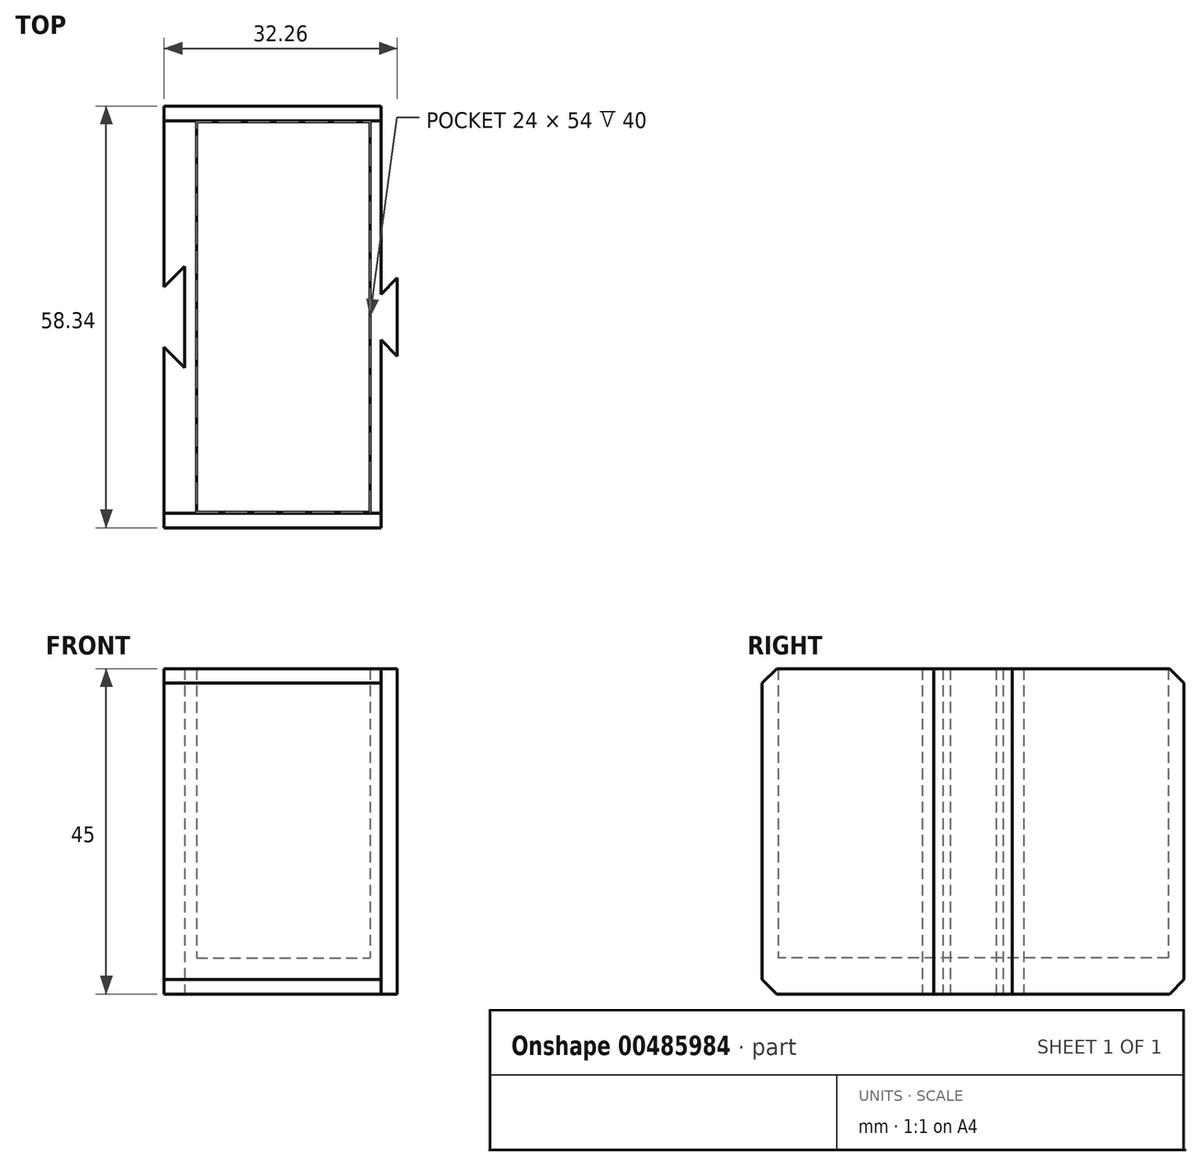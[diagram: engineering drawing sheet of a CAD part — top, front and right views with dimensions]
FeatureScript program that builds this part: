
annotation { "Feature Type Name" : "Feature", "Feature Type Description" : "" }
export const myFeature = defineFeature(function(context is Context, id is Id, definition is map)
    precondition{}
    {
        {
            var Q0;
            Q0=qCreatedBy(makeId("Top.planeOp"),FACE);
            var sketch = newSketch(context, id + "F0", { "sketchPlane" : qUnion([Q0])});
            skLineSegment(sketch, "E0", {"start": v(-15, 4.17) * mm, "end": v(-15, 29.17) * mm});
            skLineSegment(sketch, "E1", {"start": v(-15, 29.17) * mm, "end": v(15, 29.17) * mm});
            skLineSegment(sketch, "E2", {"start": v(15, 29.17) * mm, "end": v(15, 3.17) * mm});
            skLineSegment(sketch, "E3", {"start": v(-15, 4.17) * mm, "end": v(-12.17, 7) * mm});
            skLineSegment(sketch, "E4", {"start": v(-12.17, 7) * mm, "end": v(-12.17, 0) * mm});
            skLineSegment(sketch, "E5", {"start": v(15, 3.17) * mm, "end": v(17.26, 5.43) * mm});
            skLineSegment(sketch, "E6", {"start": v(17.26, 5.43) * mm, "end": v(17.26, -0.57) * mm});
            skLineSegment(sketch, "E7.MirrorCS", {"start": v(-15, -4.17) * mm, "end": v(-12.17, -7) * mm});
            skLineSegment(sketch, "E8.MirrorCS", {"start": v(15, -29.17) * mm, "end": v(15, -3.17) * mm});
            skLineSegment(sketch, "E9.MirrorCS", {"start": v(-12.17, -7) * mm, "end": v(-12.17, 0) * mm});
            skLineSegment(sketch, "E10.MirrorCS", {"start": v(-15, -4.17) * mm, "end": v(-15, -29.17) * mm});
            skLineSegment(sketch, "E11.MirrorCS", {"start": v(17.26, -5.43) * mm, "end": v(17.26, 0.57) * mm});
            skLineSegment(sketch, "E12.MirrorCS", {"start": v(15, -3.17) * mm, "end": v(17.26, -5.43) * mm});
            skLineSegment(sketch, "E13.MirrorCS", {"start": v(-15, -29.17) * mm, "end": v(15, -29.17) * mm});
            skLineSegment(sketch, "E14.bottom", {"start": v(-10.5, 27) * mm, "end": v(13.5, 27) * mm});
            skLineSegment(sketch, "E14.top", {"start": v(-10.5, -27) * mm, "end": v(13.5, -27) * mm});
            skLineSegment(sketch, "E14.left", {"start": v(-10.5, 27) * mm, "end": v(-10.5, -27) * mm});
            skLineSegment(sketch, "E14.right", {"start": v(13.5, 27) * mm, "end": v(13.5, -27) * mm});
            skPoint(sketch, "E14.middle", {"position": v(4, -0.5) * mm});
            skSolve(sketch);
        }
        {
            var Q0;
            Q0=qSketchRegion(id+"F0",true);
            extrude(context, id + "F1", {"entities" : qUnion([Q0]), "depth" : 40 * mm});
        }
        {
            var Q0;
            Q0=makeQuery(id+"F0.imprint","IMPRINT",FACE,{"disambiguationData":[TD([[makeQuery(id+"F0.imprint","IMPRINT",EDGE,{"derivedFrom":sQuery(id+"F0.wireOp",EDGE,"E0")}),-1.0]])]});
            var Q1;
            Q1=makeQuery(id+"F0.imprint","IMPRINT",FACE,{"disambiguationData":[TD([[makeQuery(id+"F0.imprint","IMPRINT",EDGE,{"derivedFrom":sQuery(id+"F0.wireOp",EDGE,"E14.bottom")}),-1.0]])]});
            extrude(context, id + "F2", {"entities" : qUnion([Q0, Q1]), "operationType" : NewBodyOperationType.ADD, "oppositeDirection" : true, "depth" : 5 * mm});
        }
        {
            var Q0;
            Q0=makeQuery(id+"F2.opExtrude","CAP_EDGE",EDGE,{"disambiguationData":[OSD([sQuery(id+"F0.wireOp",EDGE,"E13.MirrorCS")])],"isStart":false});
            var Q1;
            Q1=makeQuery(id+"F2.opExtrude","CAP_EDGE",EDGE,{"disambiguationData":[OSD([sQuery(id+"F0.wireOp",EDGE,"E1")])],"isStart":false});
            var Q2;
            Q2=makeQuery(id+"F1.opExtrude","CAP_EDGE",EDGE,{"disambiguationData":[OSD([sQuery(id+"F0.wireOp",EDGE,"E13.MirrorCS")])],"isStart":false});
            var Q3;
            Q3=makeQuery(id+"F1.opExtrude","CAP_EDGE",EDGE,{"disambiguationData":[OSD([sQuery(id+"F0.wireOp",EDGE,"E1")])],"isStart":false});
            chamfer(context, id + "F3", {"entities" : qUnion([Q0, Q1, Q2, Q3]), "width" : 2 * mm, "tangentPropagation" : true});
        }
    });
